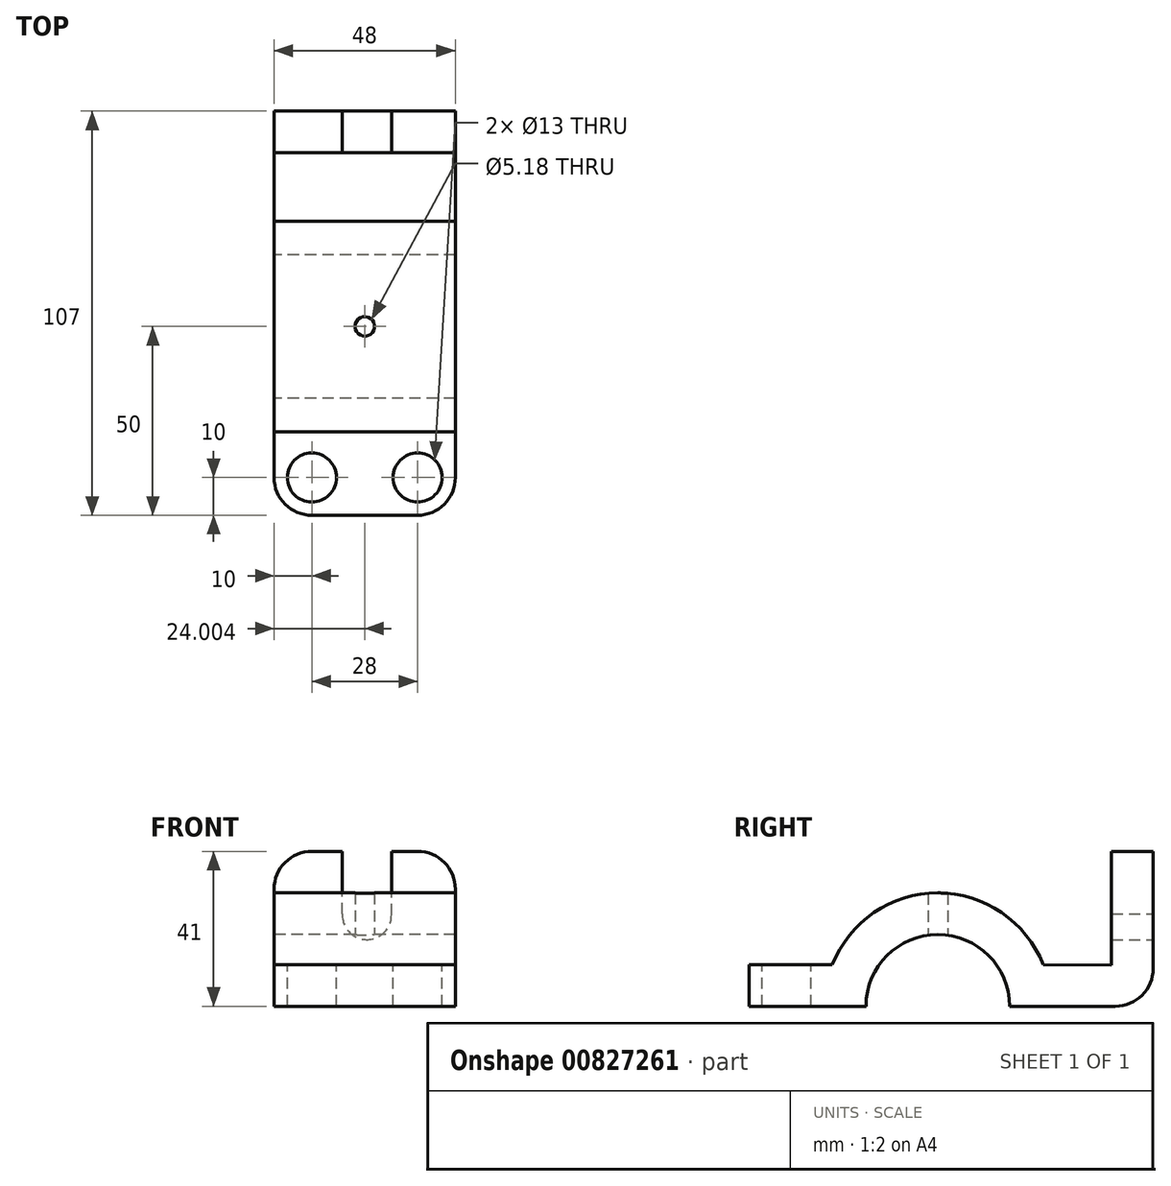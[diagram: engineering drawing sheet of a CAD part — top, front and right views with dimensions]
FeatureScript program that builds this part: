
annotation { "Feature Type Name" : "Feature", "Feature Type Description" : "" }
export const myFeature = defineFeature(function(context is Context, id is Id, definition is map)
    precondition{}
    {
        {
            var Q0;
            Q0=qCreatedBy(makeId("Right.planeOp"),FACE);
            var sketch = newSketch(context, id + "F0", { "sketchPlane" : qUnion([Q0])});
            skCircle(sketch, "E0", {"center": v(0, 0) * mm, "radius": 19 * mm});
            skCircle(sketch, "E1", {"center": v(0, 0) * mm, "radius": 30 * mm});
            skLineSegment(sketch, "E2", {"start": v(0, 0) * mm, "end": v(57, 0) * mm});
            skLineSegment(sketch, "E3", {"start": v(57, 0) * mm, "end": v(57, 41) * mm});
            skLineSegment(sketch, "E4", {"start": v(57, 41) * mm, "end": v(46, 41) * mm});
            skLineSegment(sketch, "E5", {"start": v(0, 0) * mm, "end": v(-50, 0) * mm});
            skLineSegment(sketch, "E6", {"start": v(-50, 0) * mm, "end": v(-50, 11) * mm});
            skLineSegment(sketch, "E7", {"start": v(-50, 11) * mm, "end": v(-27.91, 11) * mm});
            skLineSegment(sketch, "E8", {"start": v(27.91, 11) * mm, "end": v(44.64, 11) * mm});
            skLineSegment(sketch, "E9", {"start": v(46, 41) * mm, "end": v(46, 10.84) * mm});
            skLineSegment(sketch, "E10", {"start": v(46, 10.84) * mm, "end": v(27.91, 11) * mm});
            skSolve(sketch);
        }
        {
            var Q0;
            {var subQ0=sQuery(id+"F0.wireOp",EDGE,"E3");Q0=makeQuery(id+"F0.imprint","IMPRINT",FACE,{"disambiguationData":[TD([[makeQuery(id+"F0.imprint","IMPRINT",EDGE,{"derivedFrom":subQ0}),1.0]])]});}
            var Q1;
            {var subQ4=sQuery(id+"F0.wireOp",EDGE,"E6");Q1=makeQuery(id+"F0.imprint","IMPRINT",FACE,{"disambiguationData":[TD([[makeQuery(id+"F0.imprint","IMPRINT",EDGE,{"derivedFrom":subQ4}),-1.0]])]});}
            var Q2;
            {var subQ5=sQuery(id+"F0.wireOp",EDGE,"E2");var subQ7=sQuery(id+"F0.wireOp",EDGE,"E0");var subQ8=makeQuery(id+"F0.imprint","INTERSECT",VERTEX,{"derivedFrom":[subQ7,subQ5]});Q2=makeQuery(id+"F0.imprint","IMPRINT",FACE,{"disambiguationData":[TD([[makeQuery(id+"F0.imprint","IMPRINT",EDGE,{"disambiguationData":[TD([[subQ8,-1.0]])],"derivedFrom":subQ7}),-1.0]])]});}
            extrude(context, id + "F1", {"entities" : qUnion([Q0, Q1, Q2]), "depth" : 48 * mm, "offsetDistance" : 25 * mm});
        }
        {
            var Q0;
            Q0=makeQuery(id+"F1.opExtrude","CAP_EDGE",EDGE,{"disambiguationData":[OSD([sQuery(id+"F0.wireOp",EDGE,"E6")])],"isStart":true});
            fillet(context, id + "F2", {"entities" : qUnion([Q0]), "radius" : 10 * mm, "tangentPropagation" : true, "allowEdgeOverflow" : false});
        }
        {
            var Q0;
            Q0=makeQuery(id+"F1.opExtrude","CAP_EDGE",EDGE,{"disambiguationData":[OSD([sQuery(id+"F0.wireOp",EDGE,"E6")])],"isStart":false});
            var Q1;
            Q1=makeQuery(id+"F1.opExtrude","CAP_EDGE",EDGE,{"disambiguationData":[OSD([sQuery(id+"F0.wireOp",EDGE,"E4")])],"isStart":false});
            var Q2;
            Q2=makeQuery(id+"F1.opExtrude","CAP_EDGE",EDGE,{"disambiguationData":[OSD([sQuery(id+"F0.wireOp",EDGE,"E4")])],"isStart":true});
            var Q3;
            Q3=makeQuery(id+"F1.opExtrude","SWEPT_EDGE",EDGE,{"disambiguationData":[OSD([sQuery(id+"F0.wireOp",EDGE,"E2"),sQuery(id+"F0.wireOp",EDGE,"E3")])]});
            fillet(context, id + "F3", {"entities" : qUnion([Q0, Q1, Q2, Q3]), "radius" : 10 * mm, "tangentPropagation" : true, "allowEdgeOverflow" : false});
        }
        {
            var Q0;
            Q0=makeQuery(id+"F1.opExtrude","SWEPT_FACE",FACE,{"disambiguationData":[OSD([sQuery(id+"F0.wireOp",EDGE,"E7")])]});
            var sketch = newSketch(context, id + "F4", { "sketchPlane" : qUnion([Q0])});
            skCircle(sketch, "E11", {"center": v(10, -40) * mm, "radius": 6.5 * mm});
            skCircle(sketch, "E12", {"center": v(38, -40) * mm, "radius": 6.5 * mm});
            skSolve(sketch);
        }
        {
            var Q0;
            Q0=sQuery(id+"F4.wireOp",VERTEX,"E12.center");
            var Q1;
            Q1=sQuery(id+"F4.wireOp",VERTEX,"E11.center");
            var Q2;
            Q2=makeQuery(id+"F1.opExtrude","SWEPT_BODY",BODY,{"disambiguationData":[OSD([sQuery(id+"F0.wireOp",EDGE,"E0"),sQuery(id+"F0.wireOp",EDGE,"E1"),sQuery(id+"F0.wireOp",EDGE,"E2"),sQuery(id+"F0.wireOp",EDGE,"E3"),sQuery(id+"F0.wireOp",EDGE,"E4"),sQuery(id+"F0.wireOp",EDGE,"E5"),sQuery(id+"F0.wireOp",EDGE,"E6"),sQuery(id+"F0.wireOp",EDGE,"E7"),sQuery(id+"F0.wireOp",EDGE,"E9"),sQuery(id+"F0.wireOp",EDGE,"E10")])]});
            hole(context, id + "F5", {"style" : HoleStyle.SIMPLE, "endStyle" : HoleEndStyle.THROUGH, "holeDiameter" : 13 * mm, "majorDiameter" : 5 * mm, "isTappedThrough" : true, "tappedDepth" : 12 * mm, "tapClearance" : 3, "locations" : qUnion([Q0, Q1]), "scope" : qUnion([Q2])});
        }
        {
            var Q0;
            Q0=qCreatedBy(makeId("Top.planeOp"),FACE);
            var sketch = newSketch(context, id + "F6", { "sketchPlane" : qUnion([Q0])});
            skCircle(sketch, "E13", {"center": v(23.19, 0) * mm, "radius": 2.5 * mm});
            skSolve(sketch);
        }
        {
            var Q0;
            Q0=makeQuery(id+"F1.opExtrude","SWEPT_FACE",FACE,{"disambiguationData":[OSD([sQuery(id+"F0.wireOp",EDGE,"E3")])]});
            var sketch = newSketch(context, id + "F7", { "sketchPlane" : qUnion([Q0])});
            skArc(sketch, "E14", {"start": v(-31.07, 24.15) * mm, "mid": v(-24.43, 17.65) * mm, "end": v(-18.08, 24.43) * mm});
            skLineSegment(sketch, "E15", {"start": v(-31.07, 24.15) * mm, "end": v(-31.07, 41) * mm});
            skLineSegment(sketch, "E16", {"start": v(-18.08, 24.43) * mm, "end": v(-18.08, 41) * mm});
            skSolve(sketch);
        }
        {
            var Q0;
            Q0=makeQuery(id+"F7.imprint","IMPRINT",FACE,{"disambiguationData":[TD([[makeQuery(id+"F7.imprint","IMPRINT",EDGE,{"derivedFrom":sQuery(id+"F7.wireOp",EDGE,"E14")}),1.0]])]});
            extrude(context, id + "F8", {"entities" : qUnion([Q0]), "operationType" : NewBodyOperationType.REMOVE, "oppositeDirection" : true, "depth" : 25 * mm, "offsetDistance" : 25 * mm});
        }
        {
            var Q0;
            Q0=makeQuery(id+"F6.imprint","IMPRINT",FACE,{"disambiguationData":[TD([[makeQuery(id+"F6.imprint","IMPRINT",EDGE,{"derivedFrom":sQuery(id+"F6.wireOp",EDGE,"E13")}),1.0]])]});
            extrude(context, id + "F9", {"entities" : qUnion([Q0]), "operationType" : NewBodyOperationType.REMOVE, "oppositeDirection" : true, "depth" : 25 * mm, "offsetDistance" : 25 * mm});
        }
        {
            var Q0;
            Q0=qCreatedBy(makeId("Top.planeOp"),FACE);
            var sketch = newSketch(context, id + "F10", { "sketchPlane" : qUnion([Q0])});
            skCircle(sketch, "E17", {"center": v(24, 0) * mm, "radius": 2.59 * mm});
            skSolve(sketch);
        }
        {
            var Q0;
            Q0=makeQuery(id+"F10.imprint","IMPRINT",FACE,{"disambiguationData":[TD([[makeQuery(id+"F10.imprint","IMPRINT",EDGE,{"derivedFrom":sQuery(id+"F10.wireOp",EDGE,"E17")}),1.0]])]});
            var Q1;
            Q1=sQuery(id+"F10.wireOp",EDGE,"E17");
            extrude(context, id + "F11", {"entities" : qUnion([Q0]), "operationType" : NewBodyOperationType.REMOVE, "surfaceEntities" : qUnion([Q1]), "depth" : 35 * mm, "offsetDistance" : 25 * mm});
        }
    });
